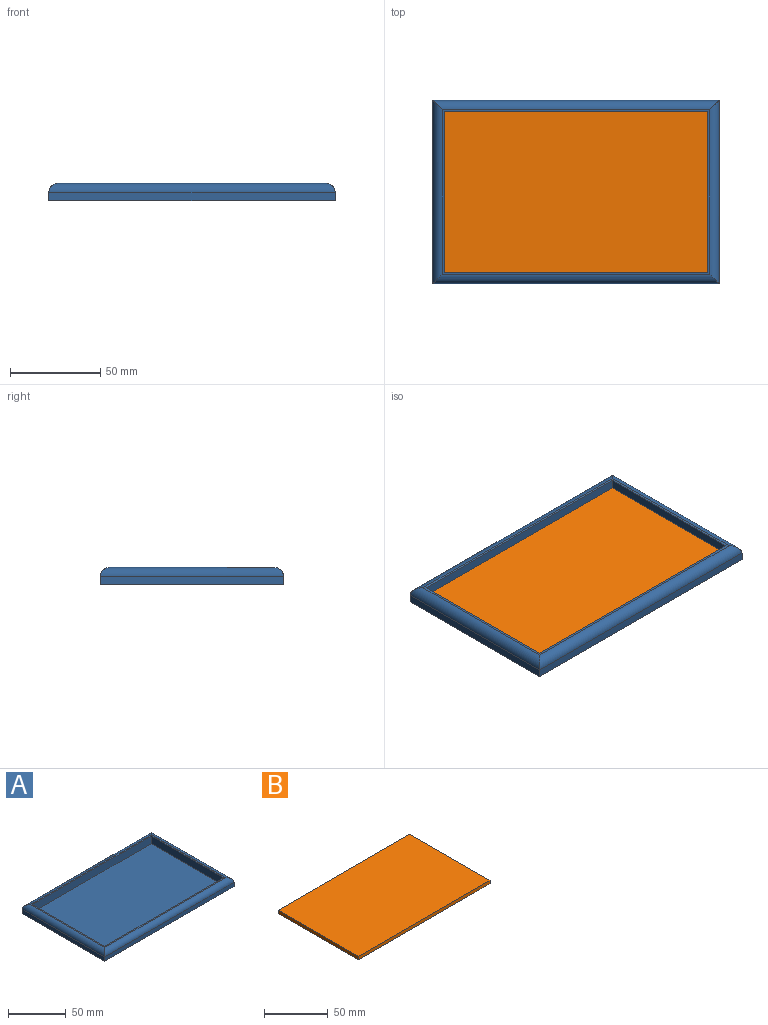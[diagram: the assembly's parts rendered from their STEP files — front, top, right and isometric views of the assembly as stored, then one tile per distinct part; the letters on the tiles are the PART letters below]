
ASSEMBLY  parts=2 mates=1
PART A: 15 faces, bbox 158.8x101.6x9.5 mm
  f0: plane 101.6x4.45mm, normal (-1,0,0), area 451.6mm2, adj f1,f7,f9,f10
  f1: plane 158.75x4.45mm, normal (0,-1,0), area 705.6mm2, adj f0,f2,f9,f11
  f2: plane 101.6x4.45mm, normal (1,0,0), area 451.6mm2, adj f1,f7,f9,f13
  f3: plane 146.05x8.26mm, normal (0,-1,0), area 1205.6mm2, adj f4,f6,f8,f14
  f4: plane 88.9x8.26mm, normal (-1,0,0), area 733.9mm2, adj f3,f5,f8,f14
  f5: plane 146.05x8.26mm, normal (0,1,0), area 1205.6mm2, adj f4,f6,f8,f14
  f6: plane 88.9x8.26mm, normal (1,0,0), area 733.9mm2, adj f3,f5,f8,f14
  f7: plane 158.75x4.45mm, normal (0,1,0), area 705.6mm2, adj f0,f2,f9,f12
  f8: plane 148.59x91.44mm, normal (0,0,1), area 603.2mm2, adj f3,f4,f5,f6,f10,f11,f12,f13
  f9: plane 158.75x101.6mm, normal (0,0,-1), area 16129mm2, adj f0,f1,f2,f7
  f10: cylinder r=5.08mm len=101.6mm, axis (0,1,0), area 781.3mm2, adj f0,f8,f11,f12
  f11: cylinder r=5.08mm len=158.75mm, axis (-1,0,0), area 1237.3mm2, adj f1,f8,f10,f13
  f12: cylinder r=5.08mm len=158.75mm, axis (1,0,0), area 1237.3mm2, adj f7,f8,f10,f13
  f13: cylinder r=5.08mm len=101.6mm, axis (0,-1,0), area 781.3mm2, adj f2,f8,f11,f12
  f14: plane 146.05x88.9mm, normal (0,0,1), area 12983.8mm2, adj f3,f4,f5,f6
PART B: 6 faces, bbox 146.1x88.9x3.2 mm
  f0: plane 88.9x3.18mm, normal (1,0,0), area 282.3mm2, adj f1,f3,f4,f5
  f1: plane 146.05x3.18mm, normal (0,1,0), area 463.7mm2, adj f0,f2,f4,f5
  f2: plane 88.9x3.18mm, normal (-1,0,0), area 282.3mm2, adj f1,f3,f4,f5
  f3: plane 146.05x3.18mm, normal (0,-1,0), area 463.7mm2, adj f0,f2,f4,f5
  f4: plane 146.05x88.9mm, normal (0,0,1), area 12983.8mm2, adj f0,f1,f2,f3
  f5: plane 146.05x88.9mm, normal (0,0,-1), area 12983.8mm2, adj f0,f1,f2,f3
PLACE A t=(-36.1,-67.43,-35.83)mm
PLACE B t=(-36.1,-67.43,-34.56)mm
MATE fastened B.f5 <-> A.f14  axis (0,0,-1) through (-36.1,-67.43,-34.56)mm
